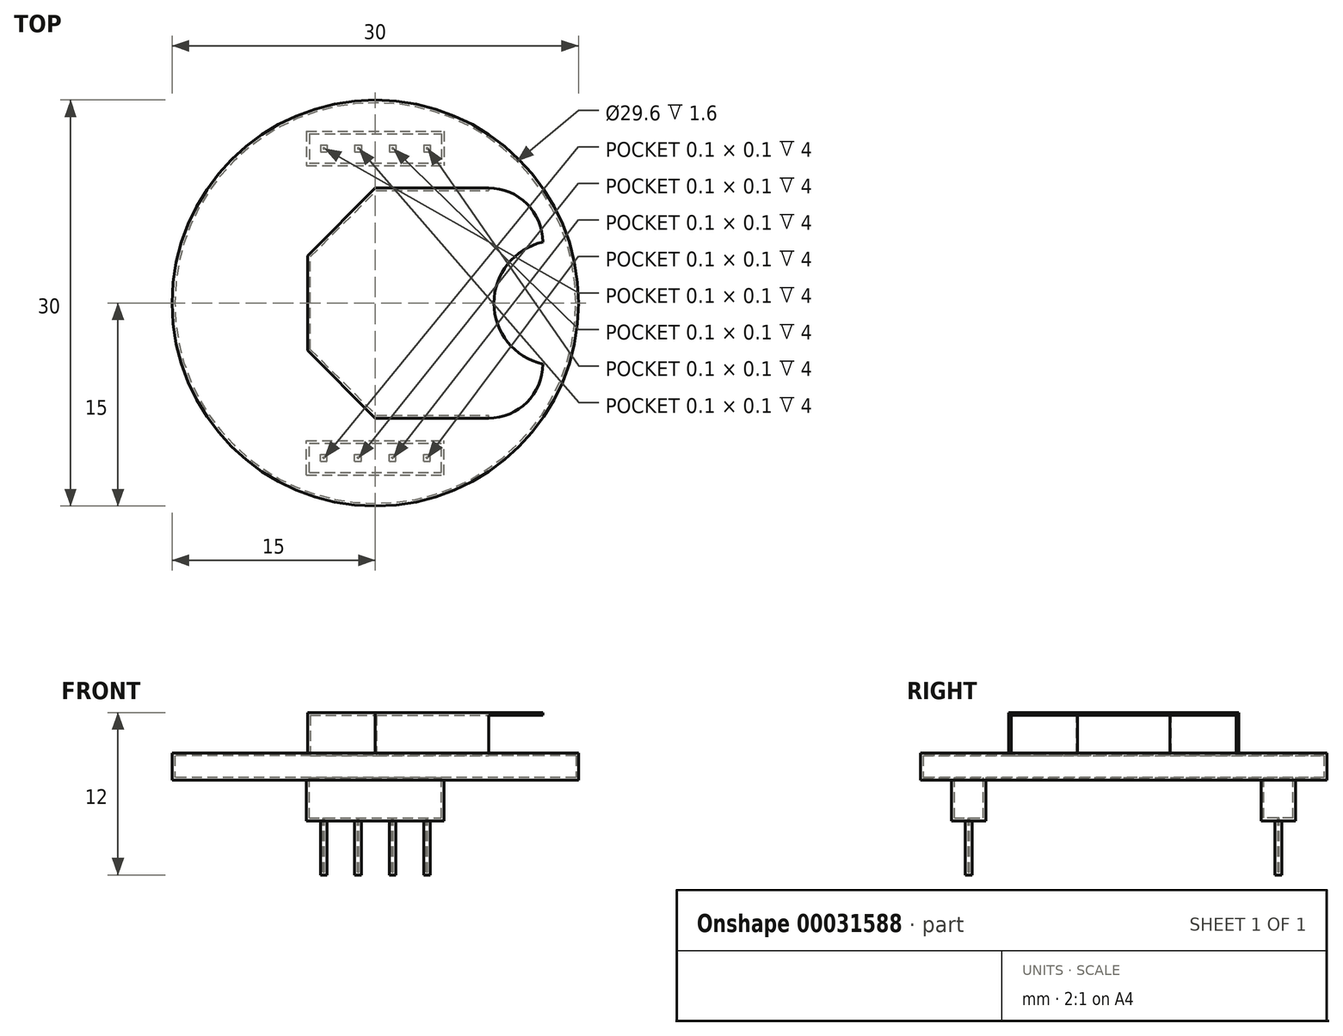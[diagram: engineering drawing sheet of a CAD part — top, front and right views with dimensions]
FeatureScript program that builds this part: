
annotation { "Feature Type Name" : "Feature", "Feature Type Description" : "" }
export const myFeature = defineFeature(function(context is Context, id is Id, definition is map)
    precondition{}
    {
        {
            var Q0;
            Q0=qCreatedBy(makeId("Top.planeOp"),FACE);
            var sketch = newSketch(context, id + "F0", { "sketchPlane" : qUnion([Q0])});
            skCircle(sketch, "E0", {"center": v(0, 0) * mm, "radius": 15 * mm});
            skSolve(sketch);
        }
        {
            var Q0;
            Q0 = qSketchRegion(id + "F0", true);
            extrude(context, id + "F1", {"entities" : qUnion([Q0]), "depth" : 2 * mm});
        }
        {
            var Q0;
            Q0=makeQuery(id+"F1.opExtrude","CAP_FACE",FACE,{"disambiguationData":[OSD([sQuery(id+"F0.wireOp",EDGE,"E0")])],"isStart":true});
            var sketch = newSketch(context, id + "F2", { "sketchPlane" : qUnion([Q0])});
            skLineSegment(sketch, "E1.bottom", {"start": v(-5.08, 12.7) * mm, "end": v(5.08, 12.7) * mm});
            skLineSegment(sketch, "E1.top", {"start": v(-5.08, 10.16) * mm, "end": v(5.08, 10.16) * mm});
            skLineSegment(sketch, "E1.left", {"start": v(-5.08, 12.7) * mm, "end": v(-5.08, 10.16) * mm});
            skLineSegment(sketch, "E1.right", {"start": v(5.08, 12.7) * mm, "end": v(5.08, 10.16) * mm});
            skLineSegment(sketch, "E2", {"start": v(0, 0) * mm, "end": v(-20, 0) * mm, "construction": true});
            skLineSegment(sketch, "E3.MirrorCS", {"start": v(-5.08, -10.16) * mm, "end": v(5.08, -10.16) * mm});
            skLineSegment(sketch, "E4.MirrorCS", {"start": v(5.08, -12.7) * mm, "end": v(5.08, -10.16) * mm});
            skLineSegment(sketch, "E5.MirrorCS", {"start": v(-5.08, -12.7) * mm, "end": v(5.08, -12.7) * mm});
            skLineSegment(sketch, "E6.MirrorCS", {"start": v(-5.08, -12.7) * mm, "end": v(-5.08, -10.16) * mm});
            skSolve(sketch);
        }
        {
            var Q0;
            Q0=makeQuery(id+"F2.imprint","IMPRINT",FACE,{"disambiguationData":[TD([[makeQuery(id+"F2.imprint","IMPRINT",EDGE,{"derivedFrom":sQuery(id+"F2.wireOp",EDGE,"E1.bottom")}),-1.0]])]});
            var Q1;
            Q1=makeQuery(id+"F2.imprint","IMPRINT",FACE,{"disambiguationData":[TD([[makeQuery(id+"F2.imprint","IMPRINT",EDGE,{"derivedFrom":sQuery(id+"F2.wireOp",EDGE,"E3.MirrorCS")}),-1.0]])]});
            extrude(context, id + "F3", {"entities" : qUnion([Q0, Q1]), "operationType" : NewBodyOperationType.ADD, "depth" : 3 * mm});
        }
        {
            var Q0;
            Q0=makeQuery(id+"F3.opExtrude","CAP_FACE",FACE,{"disambiguationData":[OSD([sQuery(id+"F2.wireOp",EDGE,"E1.bottom"),sQuery(id+"F2.wireOp",EDGE,"E1.top"),sQuery(id+"F2.wireOp",EDGE,"E1.left"),sQuery(id+"F2.wireOp",EDGE,"E1.right")])],"isStart":false});
            var sketch = newSketch(context, id + "F4", { "sketchPlane" : qUnion([Q0])});
            skLineSegment(sketch, "E7.bottom", {"start": v(-4.06, 11.68) * mm, "end": v(-3.56, 11.68) * mm});
            skLineSegment(sketch, "E7.top", {"start": v(-4.06, 11.18) * mm, "end": v(-3.56, 11.18) * mm});
            skLineSegment(sketch, "E7.left", {"start": v(-4.06, 11.68) * mm, "end": v(-4.06, 11.18) * mm});
            skLineSegment(sketch, "E7.right", {"start": v(-3.56, 11.68) * mm, "end": v(-3.56, 11.18) * mm});
            skLineSegment(sketch, "E8.bottom", {"start": v(-5.08, 12.7) * mm, "end": v(-2.54, 12.7) * mm, "construction": true});
            skLineSegment(sketch, "E8.top", {"start": v(-5.08, 10.16) * mm, "end": v(-2.54, 10.16) * mm, "construction": true});
            skLineSegment(sketch, "E8.left", {"start": v(-5.08, 12.7) * mm, "end": v(-5.08, 10.16) * mm, "construction": true});
            skLineSegment(sketch, "E8.right", {"start": v(-2.54, 12.7) * mm, "end": v(-2.54, 10.16) * mm, "construction": true});
            skLineSegment(sketch, "E9.1.0.0", {"start": v(-1.52, 11.18) * mm, "end": v(-1.02, 11.18) * mm});
            skLineSegment(sketch, "E9.1.0.1", {"start": v(-1.02, 11.68) * mm, "end": v(-1.02, 11.18) * mm});
            skLineSegment(sketch, "E9.1.0.2", {"start": v(-1.52, 11.68) * mm, "end": v(-1.02, 11.68) * mm});
            skLineSegment(sketch, "E9.1.0.3", {"start": v(-1.52, 11.68) * mm, "end": v(-1.52, 11.18) * mm});
            skLineSegment(sketch, "E9.2.0.0", {"start": v(1.02, 11.18) * mm, "end": v(1.52, 11.18) * mm});
            skLineSegment(sketch, "E9.2.0.1", {"start": v(1.52, 11.68) * mm, "end": v(1.52, 11.18) * mm});
            skLineSegment(sketch, "E9.2.0.2", {"start": v(1.02, 11.68) * mm, "end": v(1.52, 11.68) * mm});
            skLineSegment(sketch, "E9.2.0.3", {"start": v(1.02, 11.68) * mm, "end": v(1.02, 11.18) * mm});
            skLineSegment(sketch, "E9.direction1", {"start": v(-4.06, 11.18) * mm, "end": v(-1.52, 11.18) * mm, "construction": true});
            skLineSegment(sketch, "E10.0.3.0", {"start": v(3.56, 11.18) * mm, "end": v(4.06, 11.18) * mm});
            skLineSegment(sketch, "E10.3.3.0", {"start": v(4.06, 11.68) * mm, "end": v(4.06, 11.18) * mm});
            skLineSegment(sketch, "E10.6.3.0", {"start": v(3.56, 11.68) * mm, "end": v(4.06, 11.68) * mm});
            skLineSegment(sketch, "E10.9.3.0", {"start": v(3.56, 11.68) * mm, "end": v(3.56, 11.18) * mm});
            skCircle(sketch, "E11", {"center": v(-3.8, 11.43) * mm, "radius": 0.35 * mm});
            skPoint(sketch, "E11.centerSnap0", {"position": v(-3.8, 11.18) * mm});
            skPoint(sketch, "E11.centerSnap1", {"position": v(-3.56, 11.43) * mm});
            skCircle(sketch, "E12", {"center": v(-1.27, 11.43) * mm, "radius": 0.35 * mm});
            skPoint(sketch, "E12.centerSnap0", {"position": v(-1.27, 11.18) * mm});
            skPoint(sketch, "E12.centerSnap1", {"position": v(-1.02, 11.43) * mm});
            skCircle(sketch, "E13", {"center": v(1.27, 11.43) * mm, "radius": 0.35 * mm});
            skPoint(sketch, "E13.centerSnap0", {"position": v(1.27, 11.18) * mm});
            skPoint(sketch, "E13.centerSnap1", {"position": v(1.52, 11.43) * mm});
            skCircle(sketch, "E14", {"center": v(3.81, 11.43) * mm, "radius": 0.35 * mm});
            skPoint(sketch, "E14.centerSnap0", {"position": v(4.06, 11.43) * mm});
            skPoint(sketch, "E14.centerSnap1", {"position": v(3.81, 11.68) * mm});
            skLineSegment(sketch, "E15", {"start": v(0, 0) * mm, "end": v(-1.2, 0) * mm, "construction": true});
            skLineSegment(sketch, "E16.MirrorCS", {"start": v(-4.06, -11.18) * mm, "end": v(-3.56, -11.18) * mm});
            skLineSegment(sketch, "E17.MirrorCS", {"start": v(1.52, -11.68) * mm, "end": v(1.52, -11.18) * mm});
            skLineSegment(sketch, "E18.MirrorCS", {"start": v(3.56, -11.68) * mm, "end": v(4.06, -11.68) * mm});
            skLineSegment(sketch, "E19.MirrorCS", {"start": v(-3.56, -11.68) * mm, "end": v(-3.56, -11.18) * mm});
            skLineSegment(sketch, "E20.MirrorCS", {"start": v(4.06, -11.68) * mm, "end": v(4.06, -11.18) * mm});
            skLineSegment(sketch, "E21.MirrorCS", {"start": v(1.02, -11.18) * mm, "end": v(1.52, -11.18) * mm});
            skLineSegment(sketch, "E22.MirrorCS", {"start": v(-1.02, -11.68) * mm, "end": v(-1.02, -11.18) * mm});
            skLineSegment(sketch, "E23.MirrorCS", {"start": v(-4.06, -11.68) * mm, "end": v(-4.06, -11.18) * mm});
            skLineSegment(sketch, "E24.MirrorCS", {"start": v(-4.06, -11.68) * mm, "end": v(-3.56, -11.68) * mm});
            skLineSegment(sketch, "E25.MirrorCS", {"start": v(1.02, -11.68) * mm, "end": v(1.02, -11.18) * mm});
            skPoint(sketch, "E26.MirrorP", {"position": v(-3.56, -11.43) * mm});
            skLineSegment(sketch, "E27.MirrorCS", {"start": v(1.02, -11.68) * mm, "end": v(1.52, -11.68) * mm});
            skPoint(sketch, "E28.MirrorP", {"position": v(-3.8, -11.18) * mm});
            skCircle(sketch, "E29.MirrorC", {"center": v(3.81, -11.43) * mm, "radius": 0.35 * mm, "construction": true});
            skCircle(sketch, "E30.MirrorC", {"center": v(1.27, -11.43) * mm, "radius": 0.35 * mm, "construction": true});
            skPoint(sketch, "E31.MirrorP", {"position": v(3.81, -11.68) * mm});
            skCircle(sketch, "E32.MirrorC", {"center": v(-1.27, -11.43) * mm, "radius": 0.35 * mm, "construction": true});
            skCircle(sketch, "E33.MirrorC", {"center": v(-3.8, -11.43) * mm, "radius": 0.35 * mm, "construction": true});
            skPoint(sketch, "E34.MirrorP", {"position": v(1.27, -11.18) * mm});
            skPoint(sketch, "E35.MirrorP", {"position": v(-1.02, -11.43) * mm});
            skPoint(sketch, "E36.MirrorP", {"position": v(-1.27, -11.18) * mm});
            skPoint(sketch, "E37.MirrorP", {"position": v(4.06, -11.43) * mm});
            skPoint(sketch, "E38.MirrorP", {"position": v(1.52, -11.43) * mm});
            skLineSegment(sketch, "E39.MirrorCS", {"start": v(3.56, -11.68) * mm, "end": v(3.56, -11.18) * mm});
            skLineSegment(sketch, "E40.MirrorCS", {"start": v(3.56, -11.18) * mm, "end": v(4.06, -11.18) * mm});
            skLineSegment(sketch, "E41.MirrorCS", {"start": v(-1.52, -11.18) * mm, "end": v(-1.02, -11.18) * mm});
            skLineSegment(sketch, "E42.MirrorCS", {"start": v(-1.52, -11.68) * mm, "end": v(-1.52, -11.18) * mm});
            skLineSegment(sketch, "E43.MirrorCS", {"start": v(-1.52, -11.68) * mm, "end": v(-1.02, -11.68) * mm});
            skSolve(sketch);
        }
        {
            var Q0;
            Q0=makeQuery(id+"F4.imprint","IMPRINT",FACE,{"disambiguationData":[TD([[makeQuery(id+"F4.imprint","IMPRINT",EDGE,{"derivedFrom":sQuery(id+"F4.wireOp",EDGE,"E7.bottom")}),-1.0]])]});
            var Q1;
            Q1=makeQuery(id+"F4.imprint","IMPRINT",FACE,{"disambiguationData":[TD([[makeQuery(id+"F4.imprint","IMPRINT",EDGE,{"derivedFrom":sQuery(id+"F4.wireOp",EDGE,"E9.1.0.0")}),1.0]])]});
            var Q2;
            Q2=makeQuery(id+"F4.imprint","IMPRINT",FACE,{"disambiguationData":[TD([[makeQuery(id+"F4.imprint","IMPRINT",EDGE,{"derivedFrom":sQuery(id+"F4.wireOp",EDGE,"E9.2.0.0")}),1.0]])]});
            var Q3;
            Q3=makeQuery(id+"F4.imprint","IMPRINT",FACE,{"disambiguationData":[TD([[makeQuery(id+"F4.imprint","IMPRINT",EDGE,{"derivedFrom":sQuery(id+"F4.wireOp",EDGE,"E10.0.3.0")}),1.0]])]});
            var Q4;
            Q4=makeQuery(id+"F4.imprint","IMPRINT",FACE,{"disambiguationData":[TD([[makeQuery(id+"F4.imprint","IMPRINT",EDGE,{"derivedFrom":sQuery(id+"F4.wireOp",EDGE,"E16.MirrorCS")}),-1.0]])]});
            var Q5;
            Q5=makeQuery(id+"F4.imprint","IMPRINT",FACE,{"disambiguationData":[TD([[makeQuery(id+"F4.imprint","IMPRINT",EDGE,{"derivedFrom":sQuery(id+"F4.wireOp",EDGE,"E22.MirrorCS")}),1.0]])]});
            var Q6;
            Q6=makeQuery(id+"F4.imprint","IMPRINT",FACE,{"disambiguationData":[TD([[makeQuery(id+"F4.imprint","IMPRINT",EDGE,{"derivedFrom":sQuery(id+"F4.wireOp",EDGE,"E17.MirrorCS")}),1.0]])]});
            var Q7;
            Q7=makeQuery(id+"F4.imprint","IMPRINT",FACE,{"disambiguationData":[TD([[makeQuery(id+"F4.imprint","IMPRINT",EDGE,{"derivedFrom":sQuery(id+"F4.wireOp",EDGE,"E18.MirrorCS")}),1.0]])]});
            extrude(context, id + "F5", {"entities" : qUnion([Q0, Q1, Q2, Q3, Q4, Q5, Q6, Q7]), "operationType" : NewBodyOperationType.ADD, "depth" : 4 * mm});
        }
        {
            var Q0;
            Q0=makeQuery(id+"F1.opExtrude","CAP_FACE",FACE,{"disambiguationData":[OSD([sQuery(id+"F0.wireOp",EDGE,"E0")])],"isStart":false});
            var sketch = newSketch(context, id + "F6", { "sketchPlane" : qUnion([Q0])});
            skPoint(sketch, "E44.visualSharp", {"position": v(-8.5, 12.36) * mm});
            skPoint(sketch, "E45.visualSharp", {"position": v(8.5, 12.36) * mm});
            skPoint(sketch, "E46.center.orphan", {"position": v(0, 5.07) * mm});
            skPoint(sketch, "E47.visualSharp", {"position": v(-8.5, 13.09) * mm});
            skPoint(sketch, "E48.visualSharp", {"position": v(8.5, 13.09) * mm});
            skLineSegment(sketch, "E49", {"start": v(-5, -3.5) * mm, "end": v(-5, 3.5) * mm});
            skLineSegment(sketch, "E50", {"start": v(-5, 3.5) * mm, "end": v(0, 8.5) * mm});
            skLineSegment(sketch, "E51", {"start": v(-5, -3.5) * mm, "end": v(0, -8.5) * mm});
            skLineSegment(sketch, "E52", {"start": v(0, -8.5) * mm, "end": v(8.36, -8.5) * mm});
            skLineSegment(sketch, "E53", {"start": v(0, 8.5) * mm, "end": v(8.36, 8.5) * mm});
            skPoint(sketch, "E54.visualSharp", {"position": v(12.36, -8.5) * mm});
            skArc(sketch, "E54.filletArc", {"start": v(8.36, -8.5) * mm, "mid": v(11.19, -7.33) * mm, "end": v(12.36, -4.5) * mm});
            skPoint(sketch, "E55.visualSharp", {"position": v(12.36, 8.5) * mm});
            skArc(sketch, "E55.filletArc", {"start": v(12.36, 4.5) * mm, "mid": v(11.19, 7.33) * mm, "end": v(8.36, 8.5) * mm});
            skArc(sketch, "E56", {"start": v(12.36, 4.5) * mm, "mid": v(8.76, 0) * mm, "end": v(12.36, -4.5) * mm});
            skSolve(sketch);
        }
        {
            var Q0;
            Q0=makeQuery(id+"F6.imprint","IMPRINT",FACE,{"disambiguationData":[TD([[makeQuery(id+"F6.imprint","IMPRINT",EDGE,{"derivedFrom":sQuery(id+"F6.wireOp",EDGE,"E49")}),-1.0]])]});
            var Q1;
            Q1=sQuery(id+"F6.wireOp",EDGE,"c3eafaa5-0e19-4bf4-b879-9f055bbda440");
            extrude(context, id + "F7", {"entities" : qUnion([Q0]), "operationType" : NewBodyOperationType.ADD, "surfaceEntities" : qUnion([Q1]), "depth" : 3 * mm});
        }
        {
            var Q0;
            Q0=makeQuery(id+"F7.opExtrude","SWEPT_FACE",FACE,{"disambiguationData":[OSD([sQuery(id+"F6.wireOp",EDGE,"E54.filletArc")])]});
            var Q1;
            Q1=makeQuery(id+"F7.opExtrude","SWEPT_FACE",FACE,{"disambiguationData":[OSD([sQuery(id+"F6.wireOp",EDGE,"E56")])]});
            var Q2;
            Q2=makeQuery(id+"F7.opExtrude","SWEPT_FACE",FACE,{"disambiguationData":[OSD([sQuery(id+"F6.wireOp",EDGE,"E55.filletArc")])]});
            shell(context, id + "F8", {"entities" : qUnion([Q0, Q1, Q2]), "thickness" : 0.2 * mm});
        }
    });
